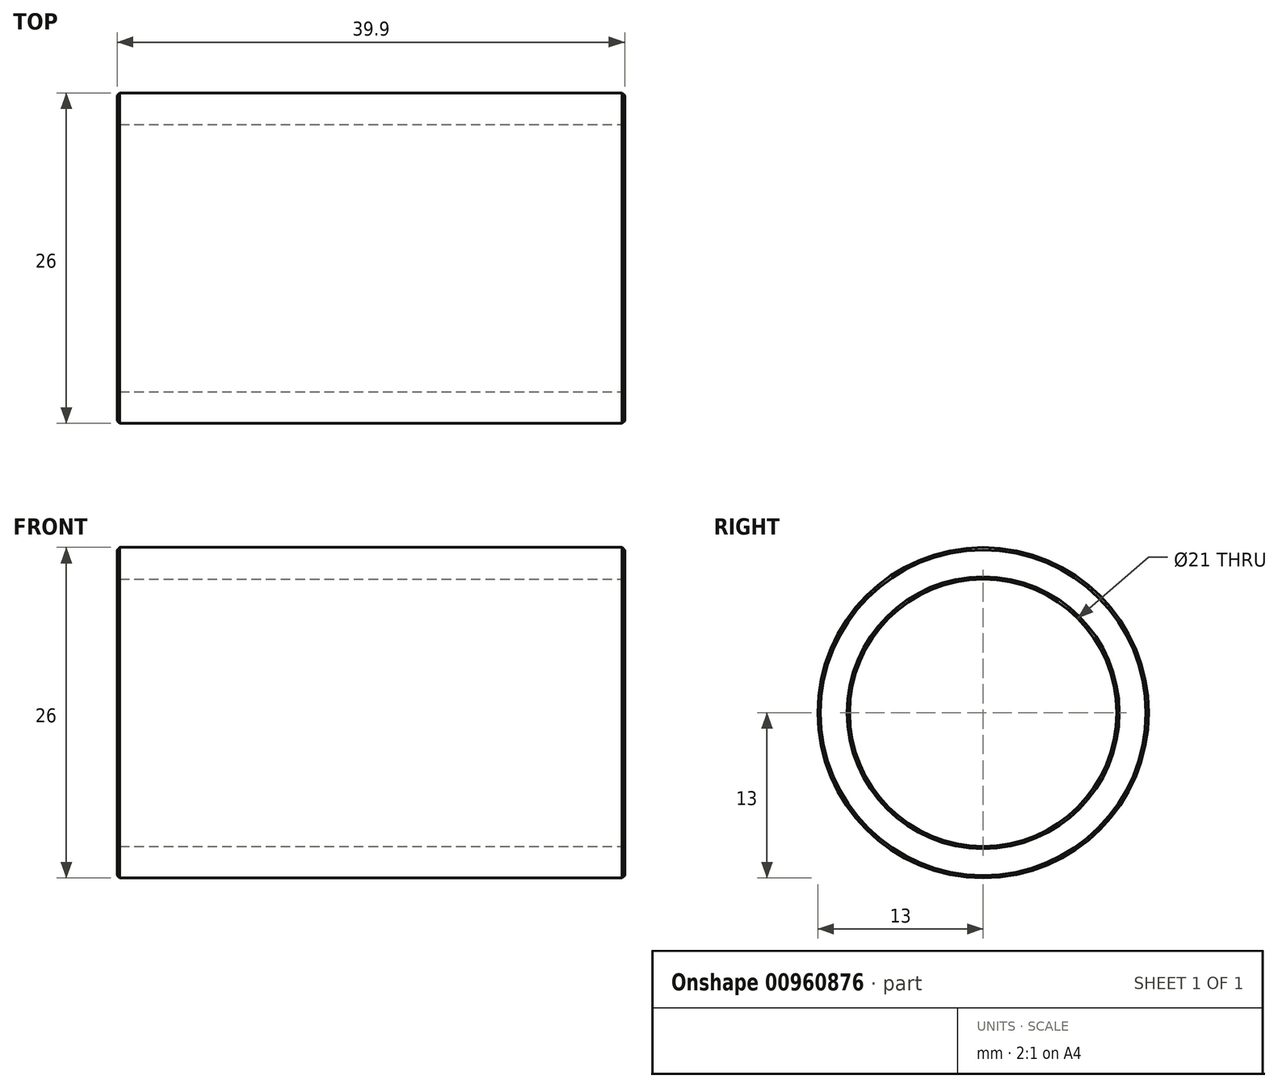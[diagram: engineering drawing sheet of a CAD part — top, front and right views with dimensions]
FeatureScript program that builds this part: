
annotation { "Feature Type Name" : "Feature", "Feature Type Description" : "" }
export const myFeature = defineFeature(function(context is Context, id is Id, definition is map)
    precondition{}
    {
        {
            var Q0;
            Q0=qCreatedBy(makeId("Front.planeOp"),FACE);
            var sketch = newSketch(context, id + "F0", { "sketchPlane" : qUnion([Q0])});
            skLineSegment(sketch, "E0.bottom", {"start": v(17.17, 13) * mm, "end": v(-22.73, 13) * mm});
            skLineSegment(sketch, "E0.top", {"start": v(17.17, 10.5) * mm, "end": v(-22.73, 10.5) * mm});
            skLineSegment(sketch, "E0.left", {"start": v(17.17, 13) * mm, "end": v(17.17, 10.5) * mm});
            skLineSegment(sketch, "E0.right", {"start": v(-22.73, 13) * mm, "end": v(-22.73, 10.5) * mm});
            skLineSegment(sketch, "E1", {"start": v(0, 0) * mm, "end": v(-9.6, 0) * mm});
            skSolve(sketch);
        }
        {
            var Q0;
            Q0=qSketchRegion(id+"F0",true);
            var Q1;
            Q1=sQuery(id+"F0.wireOp",EDGE,"E1");
            revolve(context, id + "F1", {"surfaceOperationType" : NewSurfaceOperationType.NEW, "entities" : qUnion([Q0]), "axis" : qUnion([Q1]), "revolveType" : RevolveType.FULL});
        }
        {
            var Q0;
            Q0=makeQuery(id+"F1.opRevolve","SWEPT_EDGE",EDGE,{"disambiguationData":[OSD([sQuery(id+"F0.wireOp",EDGE,"E0.bottom"),sQuery(id+"F0.wireOp",EDGE,"E0.left")])]});
            var Q1;
            Q1=makeQuery(id+"F1.opRevolve","SWEPT_EDGE",EDGE,{"disambiguationData":[OSD([sQuery(id+"F0.wireOp",EDGE,"E0.top"),sQuery(id+"F0.wireOp",EDGE,"E0.left")])]});
            var Q2;
            Q2=makeQuery(id+"F1.opRevolve","SWEPT_EDGE",EDGE,{"disambiguationData":[OSD([sQuery(id+"F0.wireOp",EDGE,"E0.top"),sQuery(id+"F0.wireOp",EDGE,"E0.right")])]});
            var Q3;
            Q3=makeQuery(id+"F1.opRevolve","SWEPT_EDGE",EDGE,{"disambiguationData":[OSD([sQuery(id+"F0.wireOp",EDGE,"E0.bottom"),sQuery(id+"F0.wireOp",EDGE,"E0.right")])]});
            chamfer(context, id + "F2", {"entities" : qUnion([Q0, Q1, Q2, Q3]), "width" : 0.2 * mm, "tangentPropagation" : true});
        }
    });
